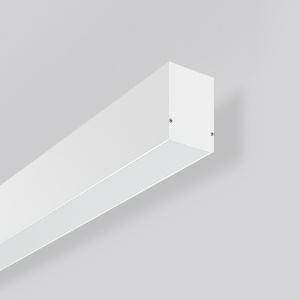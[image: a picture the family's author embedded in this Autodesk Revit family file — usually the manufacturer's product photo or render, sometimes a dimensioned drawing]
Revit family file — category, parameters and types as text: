
# Revit family: less_is_more_50_312610_002_1_76_e820
name_source: partatom
category: Lighting Fixtures
units: mm (PartAtom-declared; Revit-internal decimal feet)

## family parameters
Cut with Voids When Loaded = No
Host = Face
Light Source = No
Part Type = Normal
Room Calculation Point = No
Round Connector Dimension = Use Diameter
Shared = No

## types (1)
- LESS IS MORE 50 (1 x LED Modul 840, 3400 lm, 4000)
    Apparent Load = 25 VA
    CIE Flux Codes = 48 80 96 50 100
    Color Rendering = 80
    Color Temperature = 4000
    Default Elevation = 1800 mm
    Description = Series: LESS IS MORE 50
Linear wall luminaires. Housing: extruded aluminium profile, powder-coated. End cap aluminium powder-coated. Diffuser made of non-yellowing plastic (PMMA), opal. Direct 50%, indirect 50% light emission. Suitable for Wall (surface). LED unit with integrated converter interchangeable and removable. Suitable for through-wiring. With sensors or as a safety luminaire on request. 
Colour: traffic white, matt (RAL 9016)
Length: 1407 mm
Width: 67 mm
Height: 75 mm
Lamp: LED
Socket: without socket
Colour temperature: 4000K
Colour rendering index (CRI): 80
Light source: LED
Socket lamp2: Without base
Colour temperature: 4000K
Colour rendering index (CRI) 2: 80
System power: 25 W
Rated luminous flux: 3400 lm
Luminous efficiency: 136 lm/W
Control gear: Converter, dimmable, DALI
Control gear: Converter, dimmable, DALI
Protection class: I
Type of protection: IP 20
    Height = 75 mm
    Lamp = 1 x LED Modul 840
    Lamp Light Flux = 3400 lm
    Lamp count = 1
    Length = 1407 mm
    Lifetime = 50000 h
    Luminous efficacy = 136 lm/W
    Manufacturer = RZB
    ModVariant = No
    Model = 312610.002.1.76
    Mounting Place = Wall
    Mounting Type = Surface mounted
    Number of Poles = 1
    OnlyDefault = Yes
    Power Factor = 1
    Product Name = LESS IS MORE 50
    Product group = Surface mounted LED linear luminaires
    ProductGroupID = 2007
    Protection Class = Protection class I
    Protection Degree = IP 20
    RLX_Detail_Level = 1
    RLX_Emergency_Light_Flux = 0 lm
    RLX_Emergency_Type = 0
    RLX_Emergency_Type_DB = No
    RlxData = <blob elided: 39613 chars, md5=0fd8f8e7>
    Socket = socket
    Standby Power = 0 W
    System Light Flux = 3400 lm
    System Power = 25 W
    Type Comments = Product without accessories
    Type Image = 312606.002.jpg
    URL = http://relux.com
    VarID = ---
    Voltage = 0 V
    Weight = 0.00 kg
    Width = 67 mm

## geometry (parser evidence)
native form markers: Blend x4, Sweep x11
no freeform markers — native parametric forms only
